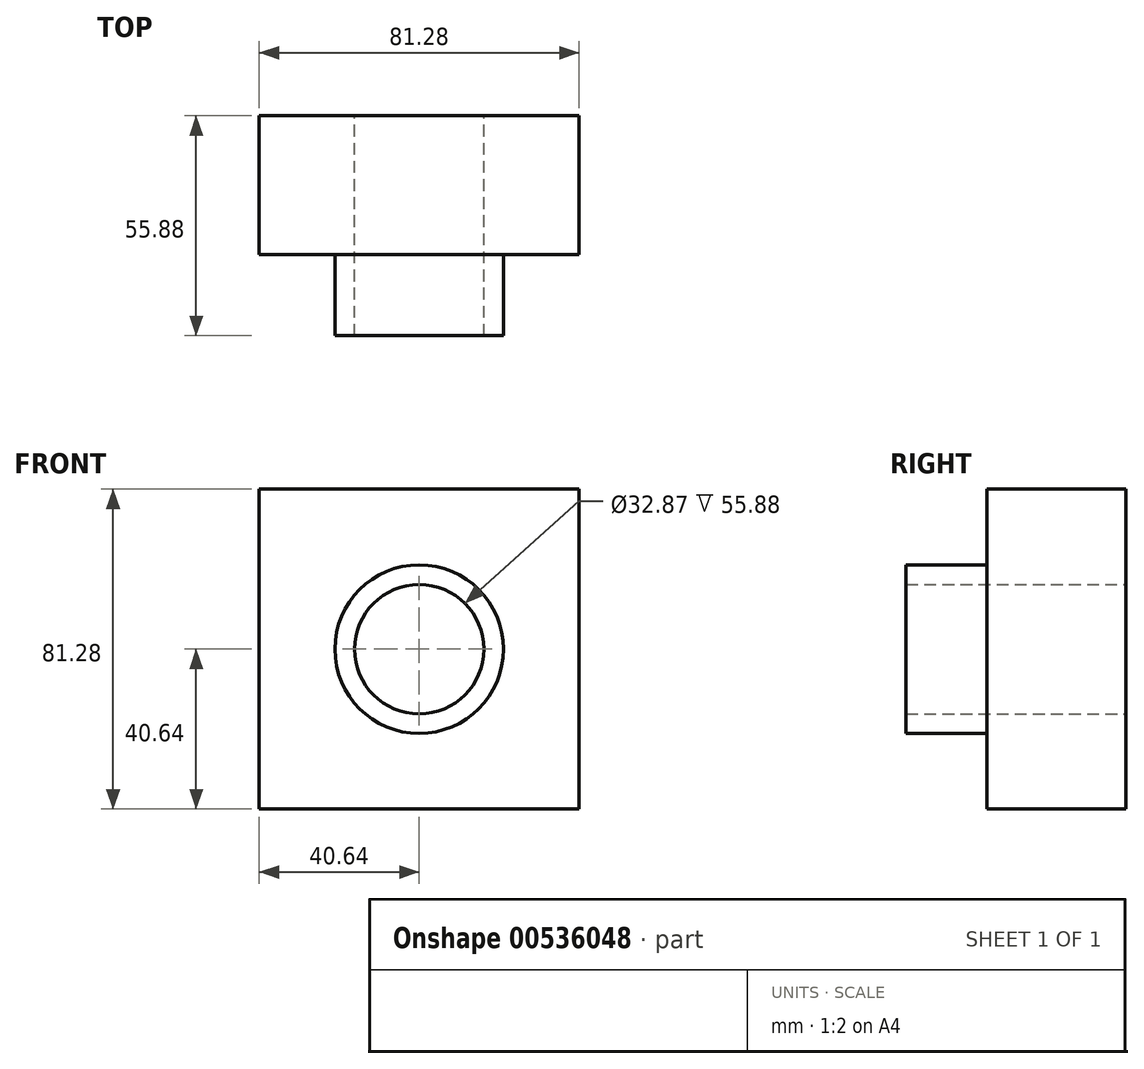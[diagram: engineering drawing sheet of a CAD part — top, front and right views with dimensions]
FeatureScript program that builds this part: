
annotation { "Feature Type Name" : "Feature", "Feature Type Description" : "" }
export const myFeature = defineFeature(function(context is Context, id is Id, definition is map)
    precondition{}
    {
        {
            var Q0;
            Q0=qCreatedBy(makeId("Front.planeOp"),FACE);
            var sketch = newSketch(context, id + "F0", { "sketchPlane" : qUnion([Q0])});
            skLineSegment(sketch, "E0.bottom", {"start": v(-40.64, 40.64) * mm, "end": v(40.64, 40.64) * mm});
            skLineSegment(sketch, "E0.top", {"start": v(-40.64, -40.64) * mm, "end": v(40.64, -40.64) * mm});
            skLineSegment(sketch, "E0.left", {"start": v(-40.64, 40.64) * mm, "end": v(-40.64, -40.64) * mm});
            skLineSegment(sketch, "E0.right", {"start": v(40.64, 40.64) * mm, "end": v(40.64, -40.64) * mm});
            skSolve(sketch);
        }
        {
            var Q0;
            Q0=makeQuery(id+"F0.imprint","IMPRINT",FACE,{"disambiguationData":[TD([[makeQuery(id+"F0.imprint","IMPRINT",EDGE,{"derivedFrom":sQuery(id+"F0.wireOp",EDGE,"E0.bottom")}),-1.0]])]});
            extrude(context, id + "F1", {"entities" : qUnion([Q0]), "depth" : 35.3 * mm, "offsetDistance" : 25.4 * mm});
        }
        {
            var Q0;
            Q0=qCreatedBy(makeId("Front.planeOp"),FACE);
            var sketch = newSketch(context, id + "F2", { "sketchPlane" : qUnion([Q0])});
            skCircle(sketch, "E1", {"center": v(0, 0) * mm, "radius": 21.4 * mm});
            skCircle(sketch, "E2", {"center": v(0, 0) * mm, "radius": 16.43 * mm});
            skSolve(sketch);
        }
        {
            var Q0;
            Q0=makeQuery(id+"F2.imprint","IMPRINT",FACE,{"disambiguationData":[TD([[makeQuery(id+"F2.imprint","IMPRINT",EDGE,{"derivedFrom":sQuery(id+"F2.wireOp",EDGE,"E2")}),1.0]])]});
            extrude(context, id + "F3", {"entities" : qUnion([Q0]), "operationType" : NewBodyOperationType.REMOVE, "depth" : 52.32 * mm, "offsetDistance" : 25.4 * mm});
        }
        {
            var Q0;
            Q0 = qSketchRegion(id + "F2", true);
            extrude(context, id + "F4", {"entities" : qUnion([Q0]), "operationType" : NewBodyOperationType.ADD, "depth" : 55.88 * mm, "offsetDistance" : 25.4 * mm});
        }
    });
